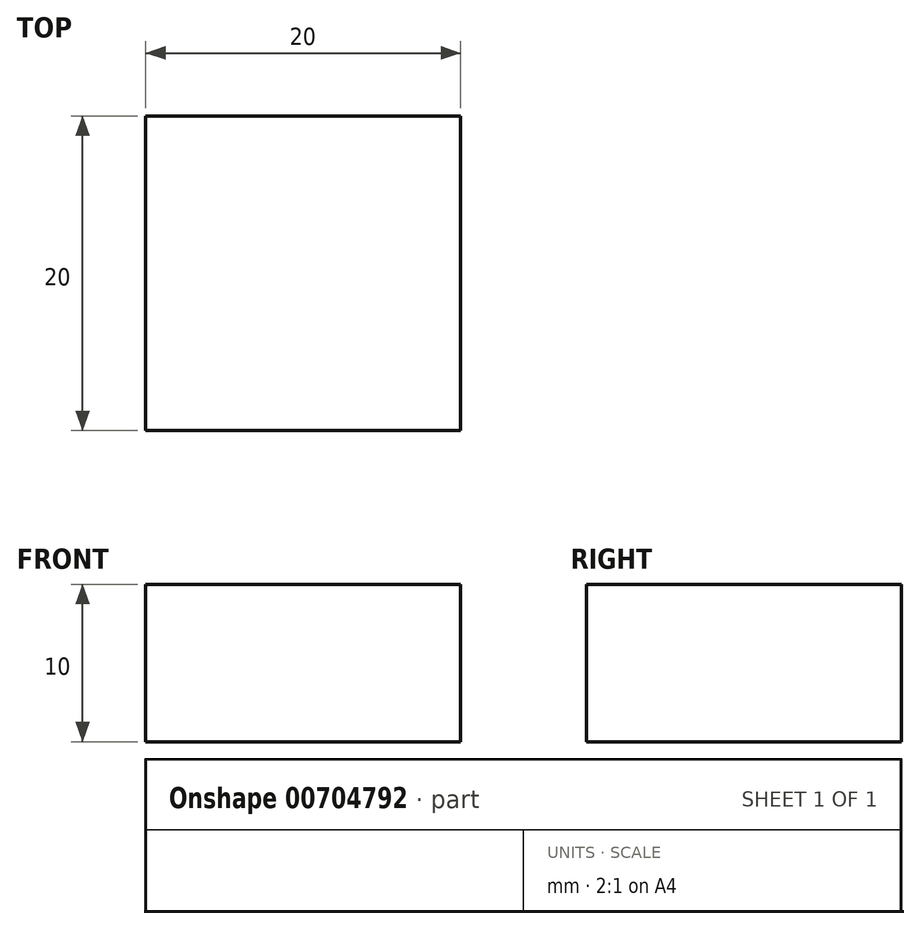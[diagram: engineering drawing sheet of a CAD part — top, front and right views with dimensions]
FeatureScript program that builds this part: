
annotation { "Feature Type Name" : "Feature", "Feature Type Description" : "" }
export const myFeature = defineFeature(function(context is Context, id is Id, definition is map)
    precondition{}
    {
        {
            var Q0;
            Q0=qCreatedBy(makeId("Top.planeOp"),FACE);
            var sketch = newSketch(context, id + "F0", { "sketchPlane" : qUnion([Q0])});
            skLineSegment(sketch, "E0.bottom", {"start": v(0, 0) * mm, "end": v(20, 0) * mm});
            skLineSegment(sketch, "E0.top", {"start": v(0, -20) * mm, "end": v(20, -20) * mm});
            skLineSegment(sketch, "E0.left", {"start": v(0, 0) * mm, "end": v(0, -20) * mm});
            skLineSegment(sketch, "E0.right", {"start": v(20, 0) * mm, "end": v(20, -20) * mm});
            skSolve(sketch);
        }
        {
            var Q0;
            Q0 = qSketchRegion(id + "F0", true);
            extrude(context, id + "F1", {"entities" : qUnion([Q0]), "depth" : 10 * mm, "offsetDistance" : 25 * mm});
        }
    });
